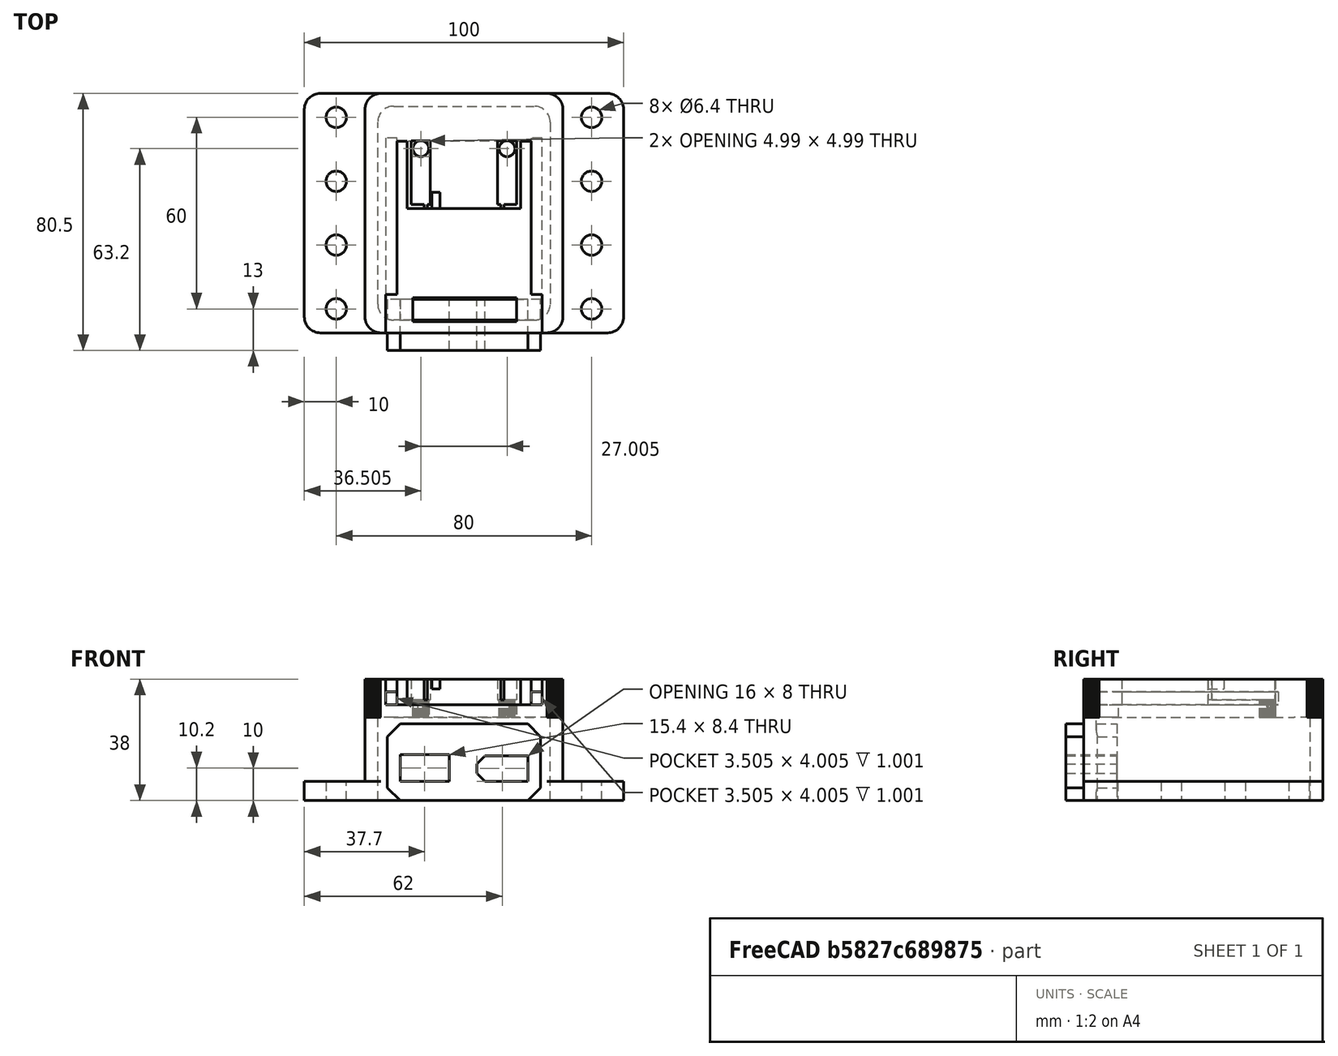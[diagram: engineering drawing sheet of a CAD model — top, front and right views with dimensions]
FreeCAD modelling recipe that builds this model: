
FCSTD DOCUMENT  (FreeCAD 0.19R17798 (Git))
Label: EinhellAdapter_raw6f
License: All rights reserved
LicenseURL: http://en.wikipedia.org/wiki/All_rights_reserved
objects: Part::Feature×4, Part::MultiFuse×3, Part::Box×1, Part::Cut×1
note: 9 computed .brp shape members not serialized (recipe doc carries the construction recipe); baked Part::Feature solids carry a one-line shape summary decoded from their .brp

FEATURE [Part::Feature] Solid
  shape: bbox 62 x 75 x 12 mm, 590 faces (baked)
FEATURE [Part::Feature] Cut001  label="addring"
  Placement = pos=(-31,-37.5,-20) rot=(0,0,1;0rad)
  shape: bbox 62 x 75 x 20 mm, 18 faces (baked)
FEATURE [Part::MultiFuse] Fusion
  Refine = true
  Shapes = -> [Solid,Cut001]
FEATURE [Part::Feature] Body001
  Placement = pos=(-50,-37.5,-26) rot=(0,0,1;0rad)
  shape: bbox 100 x 75 x 6.002 mm, 26 faces (baked)
FEATURE [Part::MultiFuse] Fusion001
  Refine = true
  Shapes = -> [Fusion,Body001]
FEATURE [Part::Feature] Body002  label="aufbau_xt60_1b_dumtest"
  Placement = pos=(24,-43,-2) rot=(0,1,0;3.14159rad)
  shape: bbox 48 x 16 x 24 mm, 20 faces (baked)
FEATURE [Part::Box] Box  label="Cube"
  AttacherType = Attacher::AttachEngine3D
  Height = 16
  Length = 44
  Placement = pos=(-22,-43,-10) rot=(-1,0,0;1.5708rad)
  Width = 12
FEATURE [Part::Cut] Cut
  Base = -> Fusion001
  Refine = true
  Tool = -> Box
FEATURE [Part::MultiFuse] Fusion002
  Refine = true
  Shapes = -> [Cut,Body002]
